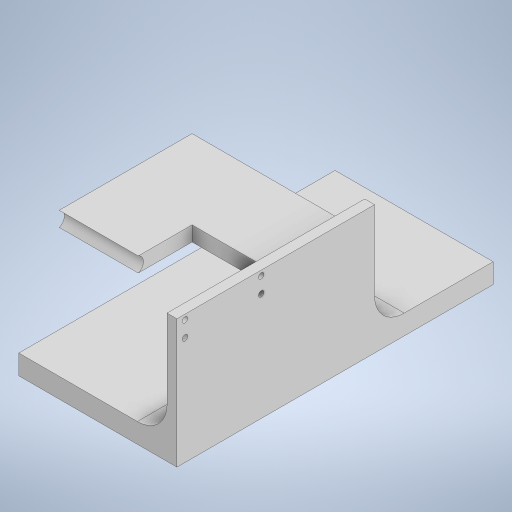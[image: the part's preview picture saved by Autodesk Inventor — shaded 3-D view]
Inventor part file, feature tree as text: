
AUTODESK INVENTOR PART (.ipt)
format: ipt  version: 2024.2 (Build 282272000, 272)  size: 279,040 bytes
history: native  units: in
note: dims shown in document units (in); Inventor stores cm internally (conversion verified against a paired STEP export)
features: extrude x7, sketch x7, fillet x2
ambient origin geometry x8: Origin, YZ Plane, XZ Plane, XY Plane, X Axis, Y Axis, Z Axis, Center Point
bodies: Solid1 (feature_tree)
feature tree (16):
  extrude  "Extrusion1"  Depth=5.0in
  extrude  "Extrusion2"  Depth=0.25in
  extrude  "Extrusion3"  Depth=0.3937in
  extrude  "Extrusion4"  Depth=1.0in TaperAngle=0.0deg
  fillet  "Fillet1"  Radius=0.138in
  fillet  "Fillet2"  Radius=1.929in
  extrude  "Extrusion5"  Depth=2.0in TaperAngle=0.0deg
  extrude  "Extrusion6"  Depth=4.0in
  extrude  "Extrusion7"  Depth=0.75in
  sketch  "Sketch1"  dims[d0=0.75in d1=5.0in]
  sketch  "Sketch2"  dims[d2=0.25in d3=0.0in d4=0.138in]
  sketch  "Sketch3"  dims[d5=0.138in d6=0.3937in]
  sketch  "Sketch4"  dims[d7=0.125in d8=1.0in d9=0.0in d11=0.138in d12=1.929in]
  sketch  "Sketch5"  dims[d13=0.138in d14=2.0in d15=0.0in]
  sketch  "Sketch6"  dims[d16=8.0in d17=4.0in]
  sketch  "Sketch7"  dims[d18=0.5in d19=0.0in d20=0.75in d21=0.75in d22=0.375in d23=2.0in d26=0.197in d27=0.25in d28=3.75in d29=0.0in d30=2.0in d31=1.5in d32=0.0in d33=0.2in d34=1.5in d35=0.0in]
